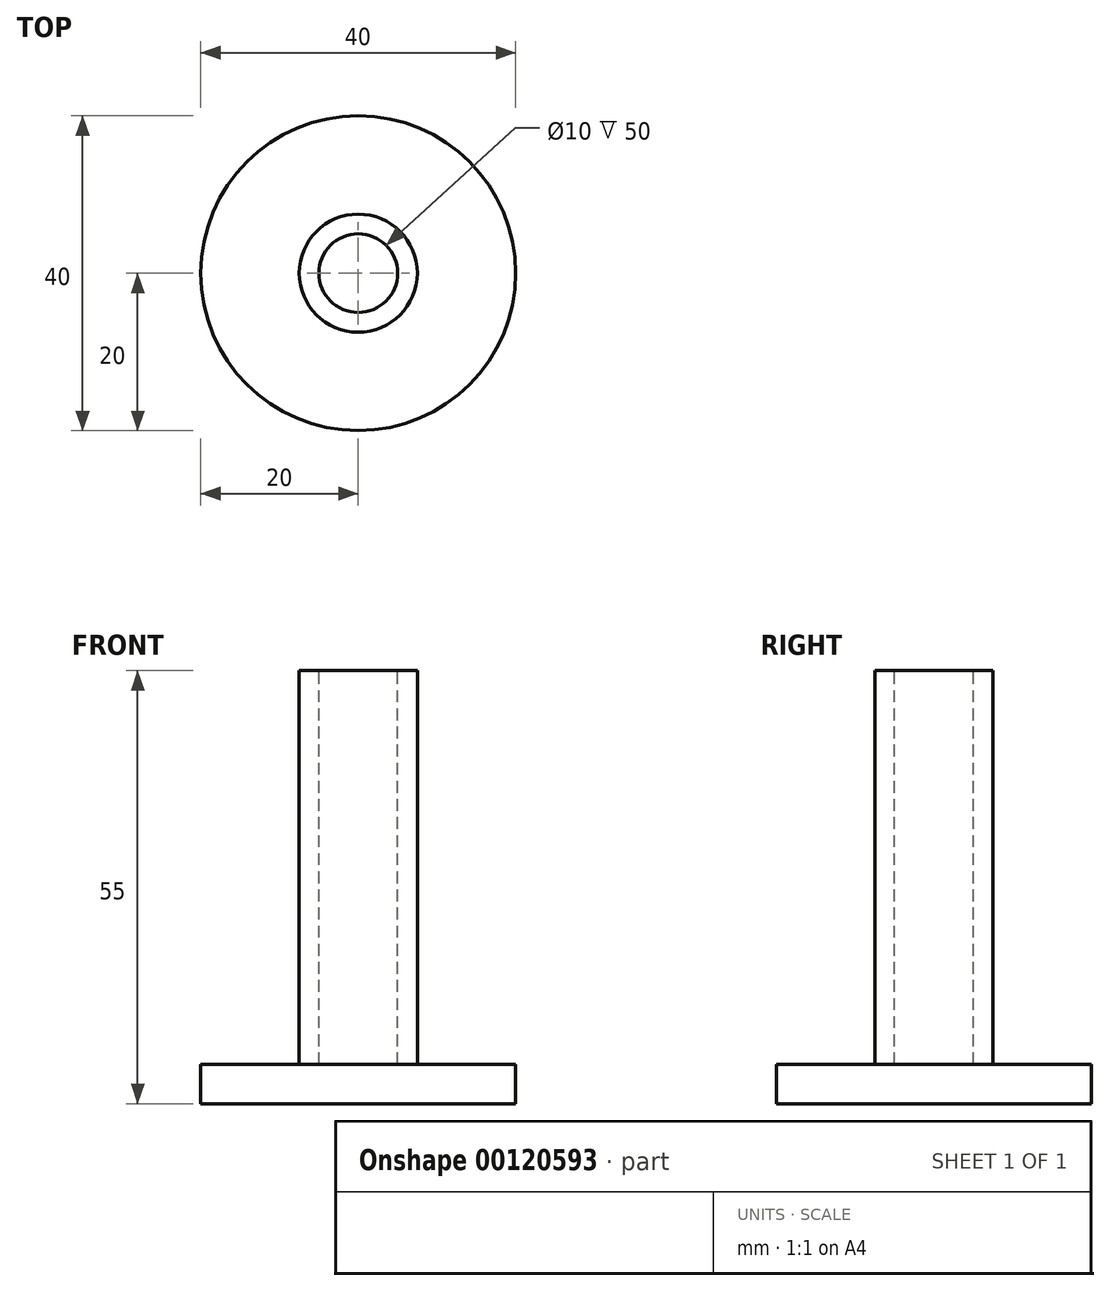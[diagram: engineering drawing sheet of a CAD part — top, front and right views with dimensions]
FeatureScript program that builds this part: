
annotation { "Feature Type Name" : "Feature", "Feature Type Description" : "" }
export const myFeature = defineFeature(function(context is Context, id is Id, definition is map)
    precondition{}
    {
        {
            var Q0;
            Q0=qCreatedBy(makeId("Front.planeOp"),FACE);
            var sketch = newSketch(context, id + "F0", { "sketchPlane" : qUnion([Q0])});
            skLineSegment(sketch, "E0", {"start": v(0, 0) * mm, "end": v(20, 0) * mm});
            skLineSegment(sketch, "E1", {"start": v(20, 0) * mm, "end": v(20, 5) * mm});
            skLineSegment(sketch, "E2", {"start": v(20, 5) * mm, "end": v(7.5, 5) * mm});
            skLineSegment(sketch, "E3", {"start": v(7.5, 5) * mm, "end": v(7.5, 55) * mm});
            skLineSegment(sketch, "E4", {"start": v(7.5, 55) * mm, "end": v(5, 55) * mm});
            skLineSegment(sketch, "E5", {"start": v(5, 55) * mm, "end": v(5, 5) * mm});
            skLineSegment(sketch, "E6", {"start": v(5, 5) * mm, "end": v(0, 5) * mm});
            skLineSegment(sketch, "E7", {"start": v(0, 5) * mm, "end": v(0, 0) * mm});
            skSolve(sketch);
        }
        {
            var Q0;
            Q0 = qSketchRegion(id + "F0", true);
            var Q1;
            Q1=sQuery(id+"F0.wireOp",EDGE,"E7");
            revolve(context, id + "F1", {"entities" : qUnion([Q0]), "axis" : qUnion([Q1]), "revolveType" : RevolveType.FULL});
        }
    });
